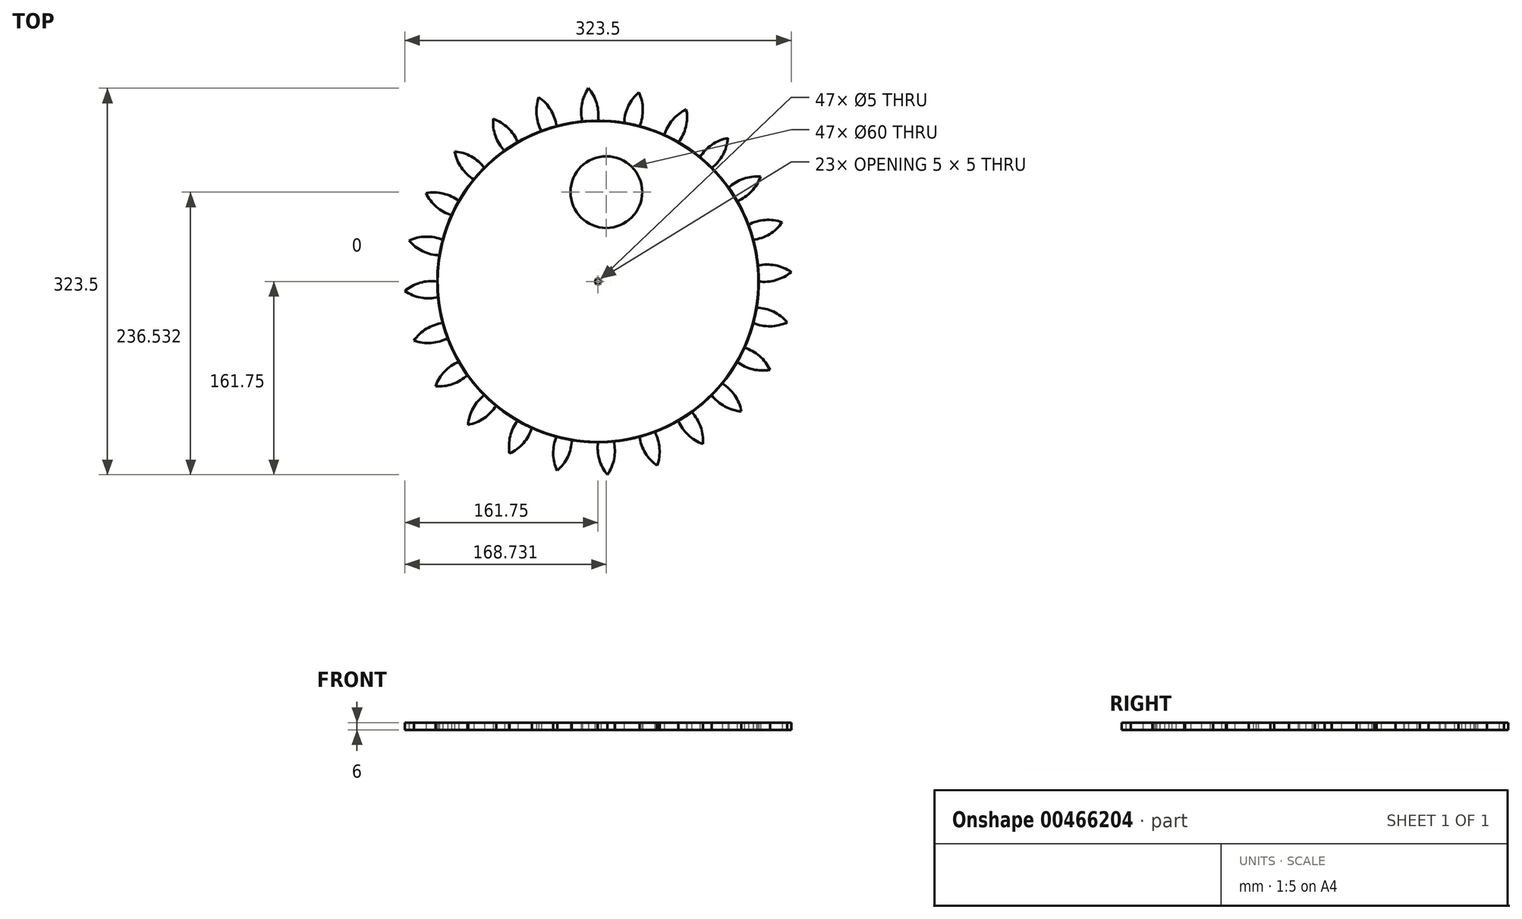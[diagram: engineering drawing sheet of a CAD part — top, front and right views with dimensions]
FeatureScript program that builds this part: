
annotation { "Feature Type Name" : "Feature", "Feature Type Description" : "" }
export const myFeature = defineFeature(function(context is Context, id is Id, definition is map)
    precondition{}
    {
        {
            var Q0;
            Q0=qCreatedBy(makeId("Top.planeOp"),FACE);
            var sketch = newSketch(context, id + "F0", { "sketchPlane" : qUnion([Q0])});
            skCircle(sketch, "E0", {"center": v(0, 0) * mm, "radius": 134.5 * mm});
            skCircle(sketch, "E1", {"center": v(0, 0) * mm, "radius": 143.38 * mm, "construction": true});
            skCircle(sketch, "E2", {"center": v(0, 0) * mm, "radius": 152.4 * mm, "construction": true});
            skLineSegment(sketch, "E3", {"start": v(0, 0) * mm, "end": v(0, 264.58) * mm, "construction": true});
            skLineSegment(sketch, "E4", {"start": v(0, 0) * mm, "end": v(-13.17, 268.12) * mm, "construction": true});
            skLineSegment(sketch, "E5", {"start": v(0, 143.38) * mm, "end": v(-191.63, 143.38) * mm, "construction": true});
            skLineSegment(sketch, "E6", {"start": v(0, 143.38) * mm, "end": v(-210.12, 65.73) * mm, "construction": true});
            skCircle(sketch, "E7", {"center": v(0, 0) * mm, "radius": 97.86 * mm, "construction": true});
            skCircle(sketch, "E8", {"center": v(0, 143.38) * mm, "radius": 35.81 * mm, "construction": true});
            skCircle(sketch, "E9", {"center": v(-35.53, 138.91) * mm, "radius": 35.81 * mm, "construction": true});
            skArc(sketch, "E10", {"start": v(0, 134.44) * mm, "mid": v(-1.07, 148.94) * mm, "end": v(-7.95, 161.75) * mm});
            skArc(sketch, "E11.MirrorCS", {"start": v(-13.18, 133.8) * mm, "mid": v(-13.53, 148.32) * mm, "end": v(-7.95, 161.75) * mm});
            skSolve(sketch);
        }
        {
            var Q0;
            {var subQ0=sQuery(id+"F0.wireOp",EDGE,"E0");var subQ1=makeQuery(id+"F0.imprint","INTERSECT",VERTEX,{"derivedFrom":[subQ0,sQuery(id+"F0.wireOp",EDGE,"E10")]});Q0=makeQuery(id+"F0.imprint","IMPRINT",FACE,{"disambiguationData":[TD([[makeQuery(id+"F0.imprint","IMPRINT",EDGE,{"disambiguationData":[TD([[subQ1,-1.0]])],"derivedFrom":subQ0}),1.0]])]});}
            var Q1;
            {var subQ0=sQuery(id+"F0.wireOp",EDGE,"E10");var subQ1=sQuery(id+"F0.wireOp",EDGE,"E0");var subQ2=makeQuery(id+"F0.imprint","INTERSECT",VERTEX,{"derivedFrom":[subQ1,subQ0]});Q1=makeQuery(id+"F0.imprint","IMPRINT",FACE,{"disambiguationData":[TD([[makeQuery(id+"F0.imprint","IMPRINT",EDGE,{"disambiguationData":[TD([[subQ2,-1.0]])],"derivedFrom":subQ1}),-1.0]])]});}
            extrude(context, id + "F1", {"entities" : qUnion([Q0, Q1]), "depth" : 6 * mm});
        }
        {
            var Q0;
            Q0=makeQuery(id+"F1.opExtrude","SWEPT_BODY",BODY,{"disambiguationData":[OSD([sQuery(id+"F0.wireOp",EDGE,"E0"),sQuery(id+"F0.wireOp",EDGE,"E10"),sQuery(id+"F0.wireOp",EDGE,"E11.MirrorCS")])]});
            var Q1;
            Q1=makeQuery(id+"F1.opExtrude","CAP_FACE",FACE,{"disambiguationData":[OSD([sQuery(id+"F0.wireOp",EDGE,"E0"),sQuery(id+"F0.wireOp",EDGE,"E10"),sQuery(id+"F0.wireOp",EDGE,"E11.MirrorCS")])],"isStart":false});
            var Q2;
            Q2=makeQuery(id+"F1.opExtrude","SWEPT_FACE",FACE,{"disambiguationData":[OSD([sQuery(id+"F0.wireOp",EDGE,"E0")])]});
            circularPattern(context, id + "F2", {"entities" : qUnion([Q0]), "axis" : qUnion([Q2]), "angle" : 360 * degree, "instanceCount" : 24, "equalSpace" : true, "isCentered" : true});
        }
        {
            var Q0;
            Q0=makeQuery(id+"F2.opPattern","COPY",FACE,{"derivedFrom":makeQuery(id+"F1.opExtrude","CAP_FACE",FACE,{"disambiguationData":[OSD([sQuery(id+"F0.wireOp",EDGE,"E0"),sQuery(id+"F0.wireOp",EDGE,"E10"),sQuery(id+"F0.wireOp",EDGE,"E11.MirrorCS")])],"isStart":true}),"instanceName":"-7"});
            var sketch = newSketch(context, id + "F3", { "sketchPlane" : qUnion([Q0])});
            skCircle(sketch, "E12", {"center": v(0, 0) * mm, "radius": 2.5 * mm});
            skSolve(sketch);
        }
        {
            var Q0;
            Q0=makeQuery(id+"F3.imprint","IMPRINT",FACE,{"disambiguationData":[TD([[makeQuery(id+"F3.imprint","IMPRINT",EDGE,{"derivedFrom":sQuery(id+"F3.wireOp",EDGE,"E12")}),1.0]])]});
            extrude(context, id + "F4", {"entities" : qUnion([Q0]), "operationType" : NewBodyOperationType.REMOVE, "endBound" : BoundingType.THROUGH_ALL, "oppositeDirection" : true, "depth" : 25 * mm});
        }
        {
            var Q0;
            Q0=makeQuery(id+"F2.opPattern","COPY",FACE,{"derivedFrom":makeQuery(id+"F1.opExtrude","CAP_FACE",FACE,{"disambiguationData":[OSD([sQuery(id+"F0.wireOp",EDGE,"E0"),sQuery(id+"F0.wireOp",EDGE,"E10"),sQuery(id+"F0.wireOp",EDGE,"E11.MirrorCS")])],"isStart":false}),"instanceName":"-17"});
            var sketch = newSketch(context, id + "F5", { "sketchPlane" : qUnion([Q0])});
            skCircle(sketch, "E13", {"center": v(0, 0) * mm, "radius": 75 * mm, "construction": true});
            skSolve(sketch);
        }
        {
            var Q0;
            {var subQ0=sQuery(id+"F0.wireOp",EDGE,"E0");Q0=makeQuery(id+"F5.imprint","IMPRINT",FACE,{"disambiguationData":[TD([[makeQuery(id+"F5.imprint","IMPRINT",EDGE,{"derivedFrom":makeQuery(id+"F2.opPattern","COPY",EDGE,{"derivedFrom":makeQuery(id+"F1.opExtrude","CAP_EDGE",EDGE,{"disambiguationData":[OSD([subQ0])],"isStart":false}),"instanceName":"-17"})}),1.0]])]});}
            var sketch = newSketch(context, id + "F6", { "sketchPlane" : qUnion([Q0])});
            skCircle(sketch, "E14", {"center": v(6.98, 74.78) * mm, "radius": 30 * mm});
            skSolve(sketch);
        }
        {
            var Q0;
            Q0 = qSketchRegion(id + "F6", true);
            extrude(context, id + "F7", {"entities" : qUnion([Q0]), "operationType" : NewBodyOperationType.REMOVE, "endBound" : BoundingType.THROUGH_ALL, "oppositeDirection" : true, "depth" : 25 * mm});
        }
    });
